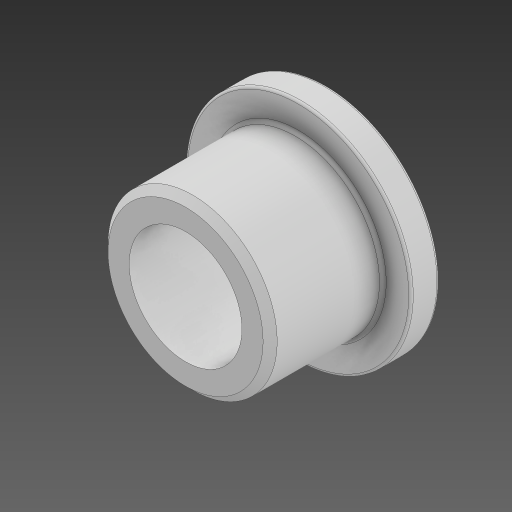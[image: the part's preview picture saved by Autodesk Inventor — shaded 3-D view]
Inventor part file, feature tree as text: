
AUTODESK INVENTOR PART (.ipt)
format: ipt  version: 2024 (Build 280153000, 153)  size: 162,816 bytes
history: native  units: in
note: dims shown in document units (in); Inventor stores cm internally (conversion verified against a paired STEP export)
features: chamfer x1
ambient origin geometry x8: Origin, YZ Plane, XZ Plane, XY Plane, X Axis, Y Axis, Z Axis, Center Point
bodies: Solid1 (feature_tree)
feature tree (1):
  chamfer  "Chamfer2"  [1 undecoded]
note: 1 required parameter value undecoded (feature->parameter linkage not recoverable at this tier; creation-order binding heuristic only, values carry confidence <= 0.55)
